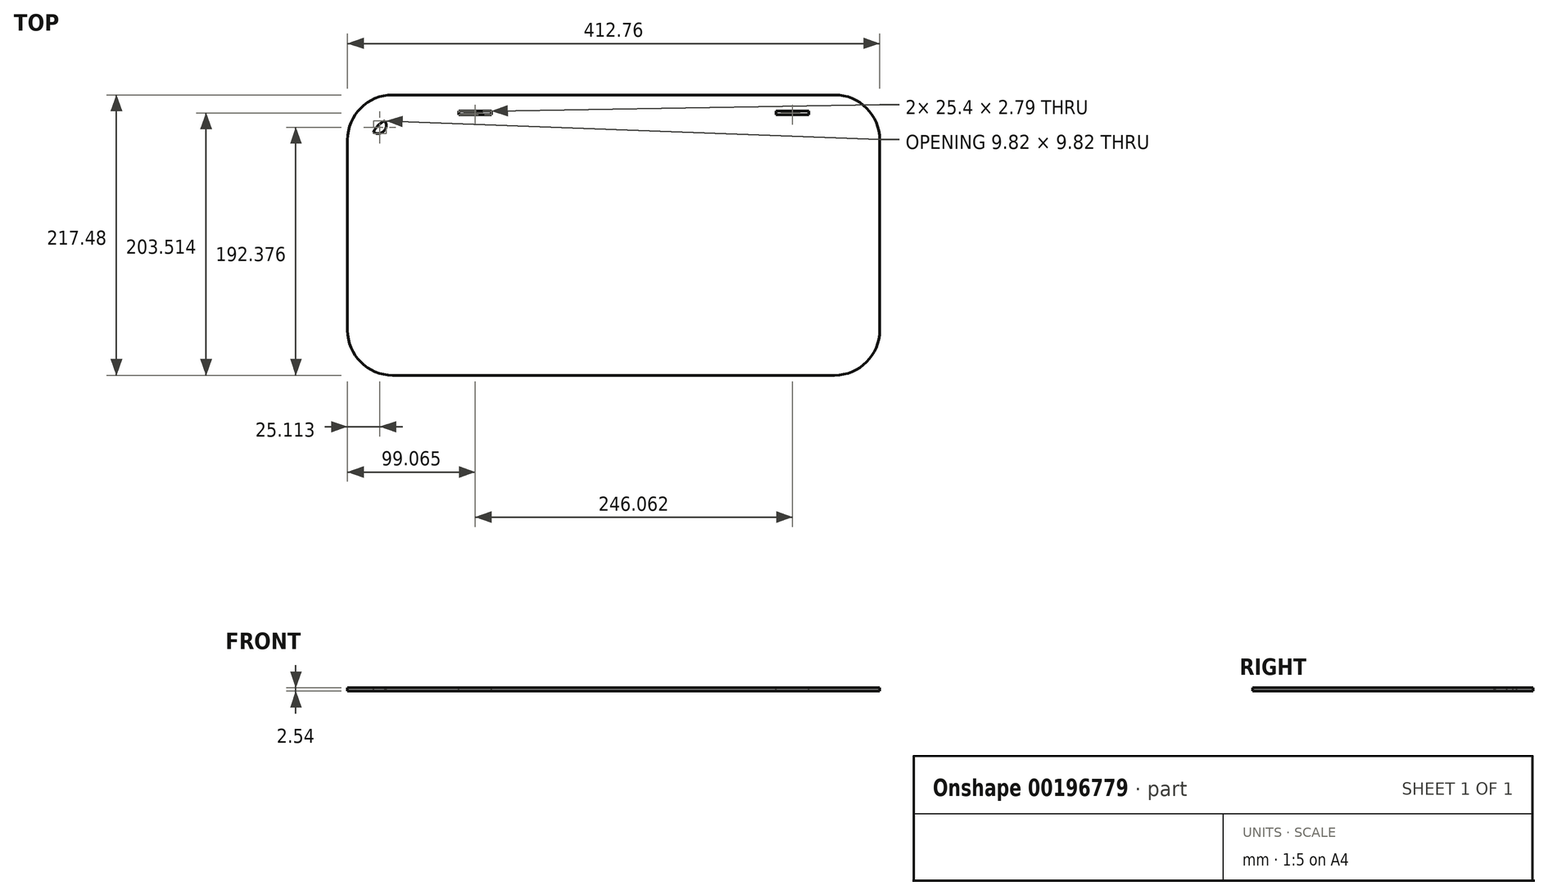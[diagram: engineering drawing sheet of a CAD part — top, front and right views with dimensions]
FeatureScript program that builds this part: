
annotation { "Feature Type Name" : "Feature", "Feature Type Description" : "" }
export const myFeature = defineFeature(function(context is Context, id is Id, definition is map)
    precondition{}
    {
        {
            var Q0;
            Q0=qCreatedBy(makeId("Top.planeOp"),FACE);
            var sketch = newSketch(context, id + "F0", { "sketchPlane" : qUnion([Q0])});
            skLineSegment(sketch, "E0.bottom", {"start": v(171.45, -89.7) * mm, "end": v(-171.45, -89.7) * mm});
            skLineSegment(sketch, "E0.top", {"start": v(171.45, 89.7) * mm, "end": v(-171.45, 89.7) * mm});
            skLineSegment(sketch, "E0.left", {"start": v(187.33, -73.82) * mm, "end": v(187.33, 73.82) * mm});
            skLineSegment(sketch, "E0.right", {"start": v(-187.32, -73.82) * mm, "end": v(-187.33, 73.82) * mm});
            skPoint(sketch, "E0.middle", {"position": v(0, 0) * mm});
            skPoint(sketch, "E1.visualSharp", {"position": v(-187.33, 89.7) * mm});
            skArc(sketch, "E1.filletArc", {"start": v(-171.45, 89.7) * mm, "mid": v(-182.68, 85.04) * mm, "end": v(-187.33, 73.82) * mm});
            skPoint(sketch, "E2.visualSharp", {"position": v(-187.33, -89.7) * mm});
            skArc(sketch, "E2.filletArc", {"start": v(-187.32, -73.82) * mm, "mid": v(-182.68, -85.04) * mm, "end": v(-171.45, -89.7) * mm});
            skPoint(sketch, "E3.visualSharp", {"position": v(187.33, -89.7) * mm});
            skArc(sketch, "E3.filletArc", {"start": v(171.45, -89.7) * mm, "mid": v(182.68, -85.04) * mm, "end": v(187.33, -73.82) * mm});
            skPoint(sketch, "E4.visualSharp", {"position": v(187.33, 89.7) * mm});
            skArc(sketch, "E4.filletArc", {"start": v(187.33, 73.82) * mm, "mid": v(182.68, 85.04) * mm, "end": v(171.45, 89.7) * mm});
            skArc(sketch, "E5.0", {"start": v(206.38, 73.82) * mm, "mid": v(196.15, 98.51) * mm, "end": v(171.45, 108.74) * mm});
            skLineSegment(sketch, "E5.1", {"start": v(206.38, -73.82) * mm, "end": v(206.38, 73.82) * mm});
            skLineSegment(sketch, "E5.2", {"start": v(171.45, 108.74) * mm, "end": v(-171.45, 108.74) * mm});
            skArc(sketch, "E5.3", {"start": v(171.45, -108.74) * mm, "mid": v(196.15, -98.51) * mm, "end": v(206.38, -73.82) * mm});
            skArc(sketch, "E5.4", {"start": v(-171.45, 108.74) * mm, "mid": v(-196.15, 98.51) * mm, "end": v(-206.38, 73.82) * mm});
            skLineSegment(sketch, "E5.5", {"start": v(-206.38, -73.82) * mm, "end": v(-206.38, 73.82) * mm});
            skArc(sketch, "E5.6", {"start": v(-206.37, -73.82) * mm, "mid": v(-196.15, -98.51) * mm, "end": v(-171.45, -108.74) * mm});
            skLineSegment(sketch, "E5.7", {"start": v(171.45, -108.74) * mm, "end": v(-171.45, -108.74) * mm});
            skSolve(sketch);
        }
        {
            var Q0;
            Q0=qSketchRegion(id+"F0",true);
            extrude(context, id + "F1", {"entities" : qUnion([Q0]), "depth" : 2.54 * mm});
        }
        {
            var Q0;
            Q0=makeQuery(id+"F1.opExtrude","CAP_FACE",FACE,{"disambiguationData":[OSD([sQuery(id+"F0.wireOp",EDGE,"E0.bottom"),sQuery(id+"F0.wireOp",EDGE,"E0.top"),sQuery(id+"F0.wireOp",EDGE,"E0.left"),sQuery(id+"F0.wireOp",EDGE,"E0.right"),sQuery(id+"F0.wireOp",EDGE,"E1.filletArc"),sQuery(id+"F0.wireOp",EDGE,"E2.filletArc"),sQuery(id+"F0.wireOp",EDGE,"E3.filletArc"),sQuery(id+"F0.wireOp",EDGE,"E4.filletArc"),sQuery(id+"F0.wireOp",EDGE,"E5.0"),sQuery(id+"F0.wireOp",EDGE,"E5.1"),sQuery(id+"F0.wireOp",EDGE,"E5.2"),sQuery(id+"F0.wireOp",EDGE,"E5.3"),sQuery(id+"F0.wireOp",EDGE,"E5.4"),sQuery(id+"F0.wireOp",EDGE,"E5.5"),sQuery(id+"F0.wireOp",EDGE,"E5.6"),sQuery(id+"F0.wireOp",EDGE,"E5.7")])],"isStart":false});
            var sketch = newSketch(context, id + "F2", { "sketchPlane" : qUnion([Q0])});
            skLineSegment(sketch, "E6.bottom", {"start": v(-136.53, 89.7) * mm, "end": v(-126.37, 89.7) * mm});
            skLineSegment(sketch, "E6.top", {"start": v(-136.53, 99.85) * mm, "end": v(-126.37, 99.85) * mm});
            skLineSegment(sketch, "E6.left", {"start": v(-136.53, 89.7) * mm, "end": v(-136.53, 99.85) * mm});
            skLineSegment(sketch, "E6.right", {"start": v(-126.37, 89.7) * mm, "end": v(-126.37, 99.85) * mm});
            skLineSegment(sketch, "E7.bottom", {"start": v(109.54, 89.7) * mm, "end": v(119.7, 89.7) * mm});
            skLineSegment(sketch, "E7.top", {"start": v(109.54, 99.85) * mm, "end": v(119.7, 99.85) * mm});
            skLineSegment(sketch, "E7.left", {"start": v(109.54, 89.7) * mm, "end": v(109.54, 99.85) * mm});
            skLineSegment(sketch, "E7.right", {"start": v(119.7, 89.7) * mm, "end": v(119.7, 99.85) * mm});
            skSolve(sketch);
        }
        {
            var Q0;
            Q0=makeQuery(id+"F1.opExtrude","CAP_FACE",FACE,{"disambiguationData":[OSD([sQuery(id+"F0.wireOp",EDGE,"E0.bottom"),sQuery(id+"F0.wireOp",EDGE,"E0.top"),sQuery(id+"F0.wireOp",EDGE,"E0.left"),sQuery(id+"F0.wireOp",EDGE,"E0.right"),sQuery(id+"F0.wireOp",EDGE,"E1.filletArc"),sQuery(id+"F0.wireOp",EDGE,"E2.filletArc"),sQuery(id+"F0.wireOp",EDGE,"E3.filletArc"),sQuery(id+"F0.wireOp",EDGE,"E4.filletArc"),sQuery(id+"F0.wireOp",EDGE,"E5.0"),sQuery(id+"F0.wireOp",EDGE,"E5.1"),sQuery(id+"F0.wireOp",EDGE,"E5.2"),sQuery(id+"F0.wireOp",EDGE,"E5.3"),sQuery(id+"F0.wireOp",EDGE,"E5.4"),sQuery(id+"F0.wireOp",EDGE,"E5.5"),sQuery(id+"F0.wireOp",EDGE,"E5.6"),sQuery(id+"F0.wireOp",EDGE,"E5.7")])],"isStart":false});
            var sketch = newSketch(context, id + "F3", { "sketchPlane" : qUnion([Q0])});
            skArc(sketch, "E8", {"start": v(-177.38, 88.55) * mm, "mid": v(-178.19, 80.55) * mm, "end": v(-186.18, 79.75) * mm});
            skArc(sketch, "E9", {"start": v(177.38, 88.55) * mm, "mid": v(178.19, 80.55) * mm, "end": v(186.18, 79.75) * mm});
            skArc(sketch, "E10", {"start": v(186.18, -79.75) * mm, "mid": v(178.19, -80.55) * mm, "end": v(177.38, -88.55) * mm});
            skArc(sketch, "E11", {"start": v(-177.38, -88.55) * mm, "mid": v(-178.19, -80.55) * mm, "end": v(-186.18, -79.75) * mm});
            skSolve(sketch);
        }
        {
            var Q0;
            {var subQ0=sQuery(id+"F3.wireOp",EDGE,"E8");Q0=makeQuery(id+"F3.imprint","IMPRINT",FACE,{"disambiguationData":[TD([[makeQuery(id+"F3.imprint","IMPRINT",EDGE,{"derivedFrom":subQ0}),-1.0]])]});}
            var Q1;
            {var subQ0=sQuery(id+"F3.wireOp",EDGE,"E9");Q1=makeQuery(id+"F3.imprint","IMPRINT",FACE,{"disambiguationData":[TD([[makeQuery(id+"F3.imprint","IMPRINT",EDGE,{"derivedFrom":subQ0}),1.0]])]});}
            var Q2;
            {var subQ0=sQuery(id+"F3.wireOp",EDGE,"E10");Q2=makeQuery(id+"F3.imprint","IMPRINT",FACE,{"disambiguationData":[TD([[makeQuery(id+"F3.imprint","IMPRINT",EDGE,{"derivedFrom":subQ0}),1.0]])]});}
            var Q3;
            {var subQ0=sQuery(id+"F3.wireOp",EDGE,"E11");Q3=makeQuery(id+"F3.imprint","IMPRINT",FACE,{"disambiguationData":[TD([[makeQuery(id+"F3.imprint","IMPRINT",EDGE,{"derivedFrom":subQ0}),1.0]])]});}
            var Q4;
            Q4=makeQuery(id+"F1.opExtrude","CAP_FACE",FACE,{"disambiguationData":[OSD([sQuery(id+"F0.wireOp",EDGE,"E0.bottom"),sQuery(id+"F0.wireOp",EDGE,"E0.top"),sQuery(id+"F0.wireOp",EDGE,"E0.left"),sQuery(id+"F0.wireOp",EDGE,"E0.right"),sQuery(id+"F0.wireOp",EDGE,"E1.filletArc"),sQuery(id+"F0.wireOp",EDGE,"E2.filletArc"),sQuery(id+"F0.wireOp",EDGE,"E3.filletArc"),sQuery(id+"F0.wireOp",EDGE,"E4.filletArc"),sQuery(id+"F0.wireOp",EDGE,"E5.0"),sQuery(id+"F0.wireOp",EDGE,"E5.1"),sQuery(id+"F0.wireOp",EDGE,"E5.2"),sQuery(id+"F0.wireOp",EDGE,"E5.3"),sQuery(id+"F0.wireOp",EDGE,"E5.4"),sQuery(id+"F0.wireOp",EDGE,"E5.5"),sQuery(id+"F0.wireOp",EDGE,"E5.6"),sQuery(id+"F0.wireOp",EDGE,"E5.7")])],"isStart":true});
            extrude(context, id + "F4", {"entities" : qUnion([Q0, Q1, Q2, Q3]), "operationType" : NewBodyOperationType.ADD, "endBound" : BoundingType.UP_TO_SURFACE, "oppositeDirection" : true, "endBoundEntityFace" : qUnion([Q4]), "depth" : 25.4 * mm});
        }
        {
            var Q0;
            Q0=makeQuery(id+"F2.imprint","IMPRINT",FACE,{"disambiguationData":[TD([[makeQuery(id+"F2.imprint","IMPRINT",EDGE,{"derivedFrom":sQuery(id+"F2.wireOp",EDGE,"E6.top")}),1.0]])]});
            var sketch = newSketch(context, id + "F5", { "sketchPlane" : qUnion([Q0])});
            skPoint(sketch, "E12.0", {"position": v(-126.37, 94.77) * mm});
            skPoint(sketch, "E13.0", {"position": v(119.7, 94.77) * mm});
            skLineSegment(sketch, "E14", {"start": v(-126.37, 94.77) * mm, "end": v(199.4, 94.77) * mm, "construction": true});
            skLineSegment(sketch, "E15.bottom", {"start": v(-94.62, 96.17) * mm, "end": v(-120.02, 96.17) * mm});
            skLineSegment(sketch, "E15.top", {"start": v(-94.62, 93.38) * mm, "end": v(-120.02, 93.38) * mm});
            skLineSegment(sketch, "E15.left", {"start": v(-94.62, 96.17) * mm, "end": v(-94.62, 93.38) * mm});
            skLineSegment(sketch, "E15.right", {"start": v(-120.02, 96.17) * mm, "end": v(-120.02, 93.38) * mm});
            skPoint(sketch, "E15.middle", {"position": v(-107.32, 94.77) * mm});
            skLineSegment(sketch, "E16.bottom", {"start": v(151.45, 96.17) * mm, "end": v(126.05, 96.17) * mm});
            skLineSegment(sketch, "E16.top", {"start": v(151.45, 93.38) * mm, "end": v(126.05, 93.38) * mm});
            skLineSegment(sketch, "E16.left", {"start": v(151.45, 96.17) * mm, "end": v(151.45, 93.38) * mm});
            skLineSegment(sketch, "E16.right", {"start": v(126.05, 96.17) * mm, "end": v(126.05, 93.38) * mm});
            skPoint(sketch, "E16.middle", {"position": v(138.75, 94.77) * mm});
            skSolve(sketch);
        }
        {
            var Q0;
            Q0 = qSketchRegion(id + "F5", true);
            extrude(context, id + "F6", {"entities" : qUnion([Q0]), "operationType" : NewBodyOperationType.REMOVE, "oppositeDirection" : true, "depth" : 25.4 * mm});
        }
    });
